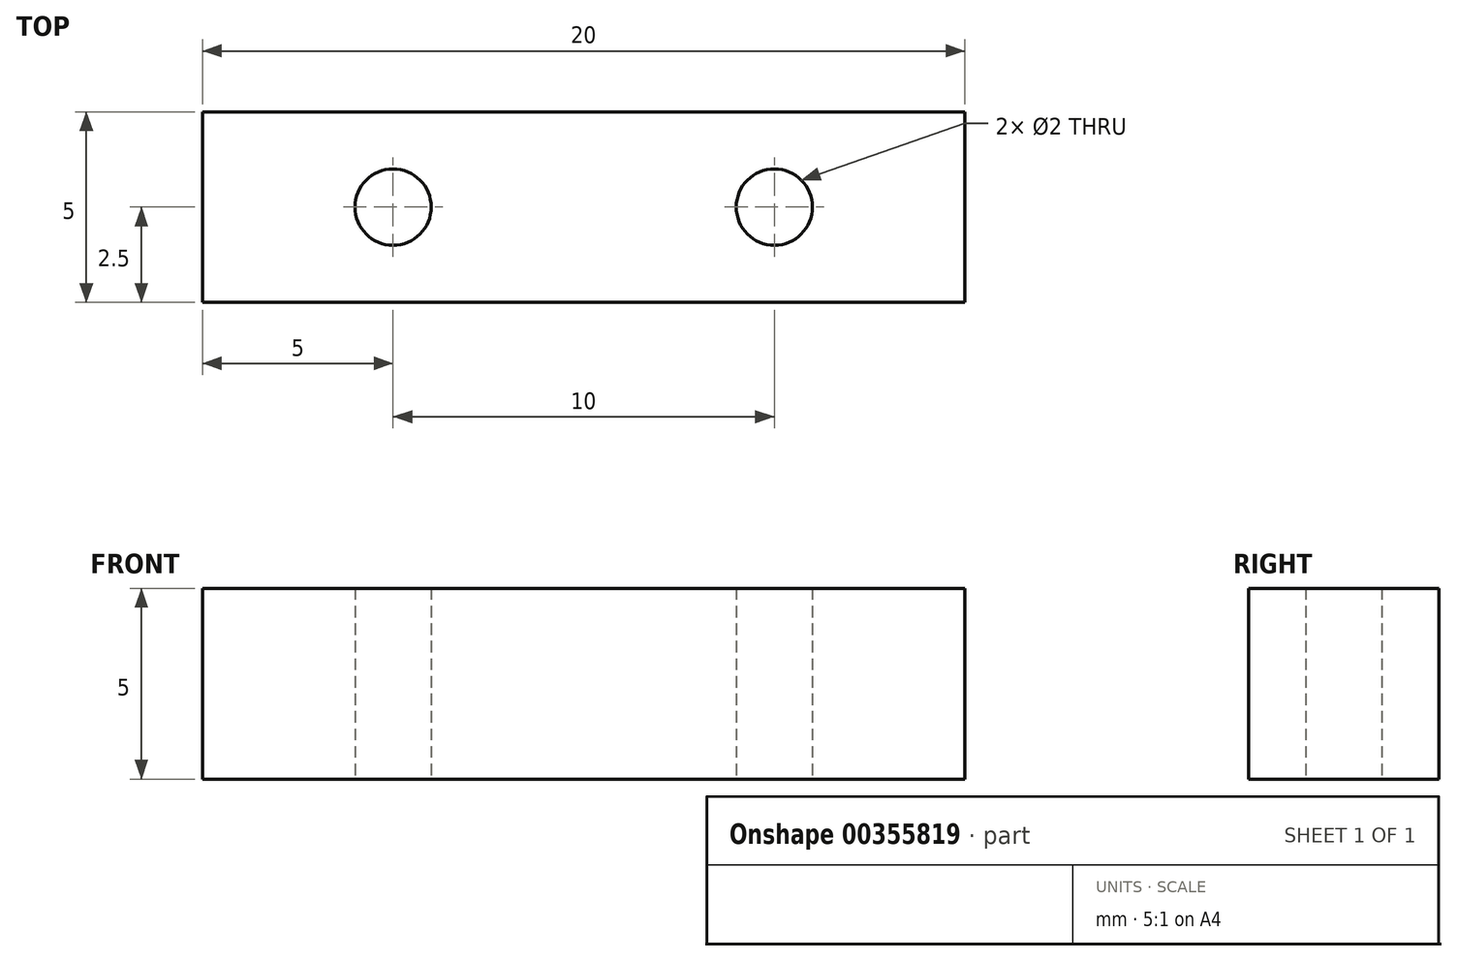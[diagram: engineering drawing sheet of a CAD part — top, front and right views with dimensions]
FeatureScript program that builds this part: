
annotation { "Feature Type Name" : "Feature", "Feature Type Description" : "" }
export const myFeature = defineFeature(function(context is Context, id is Id, definition is map)
    precondition{}
    {
        {
            var Q0;
            Q0=qCreatedBy(makeId("Front.planeOp"),FACE);
            var sketch = newSketch(context, id + "F0", { "sketchPlane" : qUnion([Q0])});
            skLineSegment(sketch, "E0.bottom", {"start": v(0, 0) * mm, "end": v(20, 0) * mm});
            skLineSegment(sketch, "E0.top", {"start": v(0, 5) * mm, "end": v(20, 5) * mm});
            skLineSegment(sketch, "E0.left", {"start": v(0, 0) * mm, "end": v(0, 5) * mm});
            skLineSegment(sketch, "E0.right", {"start": v(20, 0) * mm, "end": v(20, 5) * mm});
            skSolve(sketch);
        }
        {
            var Q0;
            Q0=qSketchRegion(id+"F0",true);
            extrude(context, id + "F1", {"entities" : qUnion([Q0]), "depth" : 5 * mm});
        }
        {
            var Q0;
            Q0=makeQuery(id+"F1.opExtrude","SWEPT_FACE",FACE,{"disambiguationData":[OSD([sQuery(id+"F0.wireOp",EDGE,"E0.bottom")])]});
            var sketch = newSketch(context, id + "F2", { "sketchPlane" : qUnion([Q0])});
            skCircle(sketch, "E1", {"center": v(15, 2.5) * mm, "radius": 1 * mm});
            skPoint(sketch, "E1.centerSnap0", {"position": v(20, 2.5) * mm});
            skCircle(sketch, "E2", {"center": v(5, 2.5) * mm, "radius": 1 * mm});
            skPoint(sketch, "E2.centerSnap0", {"position": v(0, 2.5) * mm});
            skSolve(sketch);
        }
        {
            var Q0;
            Q0=qSketchRegion(id+"F2",true);
            extrude(context, id + "F3", {"entities" : qUnion([Q0]), "operationType" : NewBodyOperationType.REMOVE, "oppositeDirection" : true, "depth" : 25 * mm});
        }
    });
